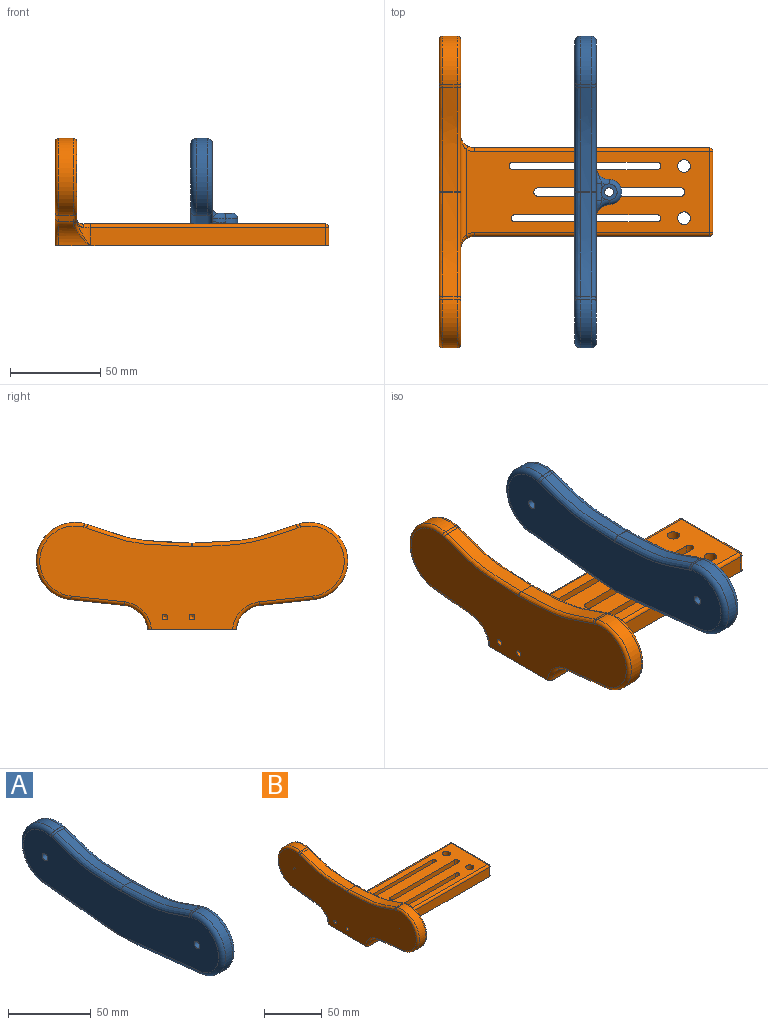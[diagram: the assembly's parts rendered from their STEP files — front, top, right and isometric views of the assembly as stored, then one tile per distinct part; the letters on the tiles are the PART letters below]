
ASSEMBLY  parts=2 mates=1
PART A: 79 faces, bbox 29.6x179.6x56 mm
  f0: plane 2.77x2.26mm, normal (0,0,1), area 2.5mm2, adj f62,f63,f74
  f1: plane 2.77x2.26mm, normal (0,0,1), area 2.5mm2, adj f62,f66,f74
  f2: plane 170.06x45.68mm, normal (1,0,0), area 5187.7mm2, adj f31,f33,f35,f39,f45,f49,f52,f54
  f3: cylinder r=2.4mm len=4.8mm, axis (1,0,0), area 67.9mm2, adj f14,f29
  f4: cylinder r=2.4mm len=4.8mm, axis (1,0,0), area 67.9mm2, adj f14,f21
  f5: cylinder r=21.5mm len=42.88mm, axis (1,0,0), area 423.5mm2, adj f13,f38,f39,f40
  f6: extruded ~6x1.63mm, area 10.2mm2, adj f7,f37,f38,f45
  f7: extruded ~57.91x10.31mm, area 355.5mm2, adj f6,f41,f48,f49
  f8: extruded ~57.91x10.31mm, area 355.5mm2, adj f9,f47,f48,f54
  f9: extruded ~6x1.63mm, area 10.2mm2, adj f8,f51,f55,f56
  f10: cylinder r=21.5mm len=42.88mm, axis (1,0,0), area 423.5mm2, adj f11,f50,f55,f58
  f11: plane 42.81x6mm, normal (0,-0.11,-0.99), area 258.3mm2, adj f10,f12,f46,f60
  f12: plane 49.61x26.59mm, normal (0,0,-1), area 685.2mm2, adj f11,f13,f32,f34,f35,f43,f46,f59
  f13: plane 42.81x6mm, normal (0,0.11,-0.99), area 258.3mm2, adj f5,f12,f35,f43
  f14: plane 167x44.13mm, normal (-1,0,0), area 5335.5mm2, adj f3,f4,f37,f40,f41,f43,f44,f46
  f15: plane 4.18x3mm, normal (0,0.03,1), area 12.6mm2, adj f16,f20,f21,f22
  f16: plane 3.56x3mm, normal (0,-0.85,0.53), area 12.6mm2, adj f15,f17,f21,f22
  f17: plane 3.68x3mm, normal (0,-0.88,-0.47), area 12.6mm2, adj f16,f18,f21,f22
  f18: plane 4.18x3mm, normal (0,-0.03,-1), area 12.6mm2, adj f17,f19,f21,f22
  f19: plane 3.56x3mm, normal (0,0.85,-0.53), area 12.6mm2, adj f18,f20,f21,f22
  f20: plane 3.68x3mm, normal (0,0.88,0.47), area 12.6mm2, adj f15,f19,f21,f22
  f21: plane 8.37x7.37mm, normal (1,0,0), area 27.4mm2, adj f4,f15,f16,f17,f18,f19,f20
  f22: plane 8.37x7.37mm, normal (-1,0,0), area 37mm2, adj f15,f16,f17,f18,f19,f20,f77
  f23: plane 4.18x3mm, normal (0,0.03,-1), area 12.6mm2, adj f24,f28,f29,f30
  f24: plane 3.68x3mm, normal (0,0.88,-0.47), area 12.6mm2, adj f23,f25,f29,f30
  f25: plane 3.56x3mm, normal (0,0.85,0.53), area 12.6mm2, adj f24,f26,f29,f30
  f26: plane 4.18x3mm, normal (0,-0.03,1), area 12.6mm2, adj f25,f27,f29,f30
  f27: plane 3.68x3mm, normal (0,-0.88,0.47), area 12.6mm2, adj f26,f28,f29,f30
  f28: plane 3.56x3mm, normal (0,-0.85,-0.53), area 12.6mm2, adj f23,f27,f29,f30
  f29: plane 8.37x7.37mm, normal (1,0,0), area 27.4mm2, adj f3,f23,f24,f25,f26,f27,f28
  f30: plane 8.37x7.37mm, normal (-1,0,0), area 37mm2, adj f23,f24,f25,f26,f27,f28,f75
  f31: cylinder r=7mm len=7mm, axis (0,0,-1), area 18.2mm2, adj f2,f32,f59,f66
  f32: cylinder r=7mm len=14mm, axis (0,0,1), area 65.3mm2, adj f12,f31,f33,f34,f59,f65
  f33: cylinder r=7mm len=7mm, axis (0,0,1), area 18.2mm2, adj f2,f32,f34,f63
  f34: bspline ~11.74x11.74mm, area 16.8mm2, adj f12,f32,f33,f35
  f35: cylinder r=3mm len=53.31mm, axis (0,0.99,0.11), area 233.2mm2, adj f2,f12,f13,f34,f39
  f36: sphere r=3mm, area 0.4mm2, adj f37,f38,f40
  f37: bspline ~3.6x3.29mm, area 8mm2, adj f6,f14,f36,f41
  f38: cylinder r=3mm len=6mm, axis (1,0,0), area 0.7mm2, adj f5,f6,f36,f42
  f39: torus R=18.5mm, axis (1,0,0), area 315.7mm2, adj f2,f5,f35,f42
  f40: torus R=18.5mm, axis (1,0,0), area 315.7mm2, adj f5,f14,f36,f43
  f41: bspline ~73.35x17.39mm, area 280.6mm2, adj f7,f14,f37,f44
  f42: sphere r=3mm, area 0.4mm2, adj f38,f39,f45
  f43: cylinder r=3mm len=67.35mm, axis (0,-0.99,-0.11), area 249.8mm2, adj f12,f13,f14,f40,f46
  f44: torus R=6mm, axis (1,0,0), area 0.7mm2, adj f14,f41,f47,f48
  f45: bspline ~3.6x3.29mm, area 8mm2, adj f2,f6,f42,f49
  f46: cylinder r=3mm len=67.35mm, axis (0,-0.99,0.11), area 249.8mm2, adj f11,f12,f14,f43,f50
  f47: bspline ~73.35x17.39mm, area 280.6mm2, adj f8,f14,f44,f51
  f48: cylinder r=3mm len=6mm, axis (1,0,0), area 0.7mm2, adj f7,f8,f44,f52
  f49: bspline ~73.35x17.39mm, area 280.6mm2, adj f2,f7,f45,f52
  f50: torus R=18.5mm, axis (1,0,0), area 315.7mm2, adj f10,f14,f46,f53
  f51: bspline ~3.6x3.29mm, area 8mm2, adj f9,f14,f47,f53
  f52: torus R=6mm, axis (1,0,0), area 0.7mm2, adj f2,f48,f49,f54
  f53: sphere r=3mm, area 0.4mm2, adj f50,f51,f55
  f54: bspline ~73.35x17.39mm, area 280.6mm2, adj f2,f8,f52,f56
  f55: cylinder r=3mm len=6mm, axis (1,0,0), area 0.7mm2, adj f9,f10,f53,f57
  f56: bspline ~3.6x3.29mm, area 8mm2, adj f2,f9,f54,f57
  f57: sphere r=3mm, area 0.4mm2, adj f55,f56,f58
  f58: torus R=18.5mm, axis (1,0,0), area 315.7mm2, adj f2,f10,f57,f60
  f59: bspline ~8.63x7.79mm, area 16.8mm2, adj f12,f31,f32,f60
  f60: cylinder r=3mm len=53.31mm, axis (0,0.99,-0.11), area 233.2mm2, adj f2,f11,f12,f58,f59
  f61: bspline ~9.6x6mm, area 17.3mm2, adj f2,f62,f63
  f62: cylinder r=3mm len=9.67mm, axis (0,-1,0), area 45.6mm2, adj f0,f1,f2,f61,f64,f72
  f63: torus R=10mm, axis (0,0,1), area 30.5mm2, adj f0,f33,f61,f65,f74
  f64: bspline ~10.85x6mm, area 15.9mm2, adj f2,f62,f66
  f65: torus R=4mm, axis (0,0,1), area 80.8mm2, adj f32,f63,f66,f74
  f66: torus R=10mm, axis (0,0,1), area 30.5mm2, adj f1,f31,f64,f65,f74
  f67: cone r=0mm half-angle=59deg, axis (0,0,-1), area 5.7mm2, adj f68
  f68: cylinder r=1.25mm len=20mm, axis (0,0,-1), area 157.1mm2, adj f12,f67
  f69: cone r=0mm half-angle=59deg, axis (0,0,-1), area 5.7mm2, adj f70
  f70: cylinder r=1.25mm len=20mm, axis (0,0,-1), area 157.1mm2, adj f12,f69
  f71: cylinder r=2.4mm len=4.8mm, axis (0,0,1), area 30.2mm2, adj f12,f73
  f72: plane 4.12x0.5mm, normal (0,0,-1), area 1.4mm2, adj f62,f74
  f73: plane 9x9mm, normal (0,0,1), area 45.5mm2, adj f71,f74
  f74: cylinder r=4.5mm len=9mm, axis (0,0,1), area 112.4mm2, adj f0,f1,f63,f65,f66,f72,f73
  f75: cylinder r=1.65mm len=3.75mm, axis (1,0,0), area 38.9mm2, adj f30,f76
  f76: plane 3.3x3.3mm, normal (-1,0,0), area 8.6mm2, adj f75
  f77: cylinder r=1.65mm len=3.75mm, axis (1,0,0), area 38.9mm2, adj f22,f78
  f78: plane 3.3x3.3mm, normal (-1,0,0), area 8.6mm2, adj f77
PART B: 119 faces, bbox 152.2x176.7x62.8 mm
  f0: plane 152.18x49.18mm, normal (0,0,-1), area 5791.1mm2, adj f22,f44,f45,f46,f47,f48,f52,f53
  f1: plane 80.1x8.8mm, normal (0,-1,0), area 704.9mm2, adj f2,f4,f13,f68
  f2: cylinder r=2mm len=8.8mm, axis (0,0,-1), area 55.3mm2, adj f1,f3,f13,f68
  f3: plane 80.1x8.8mm, normal (0,1,0), area 704.9mm2, adj f2,f4,f13,f68
  f4: cylinder r=2mm len=8.8mm, axis (0,0,-1), area 55.3mm2, adj f1,f3,f13,f68
  f5: cylinder r=2.4mm len=8.8mm, axis (0,0,-1), area 66.4mm2, adj f6,f8,f13,f63
  f6: plane 79x8.8mm, normal (0,1,0), area 695.2mm2, adj f5,f7,f13,f63
  f7: cylinder r=2.4mm len=8.8mm, axis (0,0,-1), area 66.4mm2, adj f6,f8,f13,f63
  f8: plane 79x8.8mm, normal (0,-1,0), area 695.2mm2, adj f5,f7,f13,f63
  f9: plane 79x8.8mm, normal (0,-1,0), area 695.2mm2, adj f10,f12,f13,f58
  f10: cylinder r=2mm len=8.8mm, axis (0,0,-1), area 55.3mm2, adj f9,f11,f13,f58
  f11: plane 79x8.8mm, normal (0,1,0), area 695.2mm2, adj f10,f12,f13,f58
  f12: cylinder r=2mm len=8.8mm, axis (0,0,-1), area 55.3mm2, adj f9,f11,f13,f58
  f13: plane 135x47.27mm, normal (0,0,1), area 4942.5mm2, adj f1,f2,f3,f4,f5,f6,f7,f8
  f14: extruded ~57.92x10.32mm, area 474.1mm2, adj f15,f80,f84,f85
  f15: extruded ~8x1.65mm, area 13.7mm2, adj f14,f77,f78,f81
  f16: cylinder r=21.5mm len=42.88mm, axis (1,0,0), area 564.8mm2, adj f17,f73,f76,f77
  f17: plane 29.49x8mm, normal (0,-0.11,-0.99), area 237.3mm2, adj f16,f47,f71,f74
  f18: plane 29.49x8mm, normal (0,0.11,-0.99), area 237.3mm2, adj f19,f48,f87,f97
  f19: cylinder r=21.5mm len=42.88mm, axis (1,0,0), area 564.8mm2, adj f18,f90,f94,f96
  f20: extruded ~8x1.65mm, area 13.7mm2, adj f21,f89,f93,f94
  f21: extruded ~57.92x10.32mm, area 474.1mm2, adj f20,f85,f86,f91
  f22: plane 169x57.5mm, normal (-1,0,0), area 6397.8mm2, adj f0,f69,f71,f73,f78,f80,f82,f83
  f23: plane 169x43.68mm, normal (1,0,0), area 5600.3mm2, adj f24,f25,f49,f50,f51,f72,f74,f76
  f24: cylinder r=2.4mm len=4.8mm, axis (1,0,0), area 67.9mm2, adj f23,f33
  f25: cylinder r=2.4mm len=4.8mm, axis (1,0,0), area 67.9mm2, adj f23,f42
  f26: plane 4.18x3mm, normal (0,0.03,-1), area 12.6mm2, adj f27,f31,f32,f33
  f27: plane 3.68x3mm, normal (0,0.88,-0.47), area 12.6mm2, adj f26,f28,f32,f33
  f28: plane 3.56x3mm, normal (0,0.85,0.53), area 12.6mm2, adj f27,f29,f32,f33
  f29: plane 4.18x3mm, normal (0,-0.03,1), area 12.6mm2, adj f28,f30,f32,f33
  f30: plane 3.68x3mm, normal (0,-0.88,0.47), area 12.6mm2, adj f29,f31,f32,f33
  f31: plane 3.56x3mm, normal (0,-0.85,-0.53), area 12.6mm2, adj f26,f30,f32,f33
  f32: plane 8.37x7.37mm, normal (1,0,0), area 27.4mm2, adj f26,f27,f28,f29,f30,f31,f34
  f33: plane 8.37x7.37mm, normal (-1,0,0), area 27.4mm2, adj f24,f26,f27,f28,f29,f30,f31
  f34: cone r=0mm half-angle=59deg, axis (1,0,0), area 11.1mm2, adj f32,f117
  f35: plane 4.18x3mm, normal (0,0.03,1), area 12.6mm2, adj f36,f40,f41,f42
  f36: plane 3.56x3mm, normal (0,-0.85,0.53), area 12.6mm2, adj f35,f37,f41,f42
  f37: plane 3.68x3mm, normal (0,-0.88,-0.47), area 12.6mm2, adj f36,f38,f41,f42
  f38: plane 4.18x3mm, normal (0,-0.03,-1), area 12.6mm2, adj f37,f39,f41,f42
  f39: plane 3.56x3mm, normal (0,0.85,-0.53), area 12.6mm2, adj f38,f40,f41,f42
  f40: plane 3.68x3mm, normal (0,0.88,0.47), area 12.6mm2, adj f35,f39,f41,f42
  f41: plane 8.37x7.37mm, normal (1,0,0), area 27.4mm2, adj f35,f36,f37,f38,f39,f40,f43
  f42: plane 8.37x7.37mm, normal (-1,0,0), area 27.4mm2, adj f25,f35,f36,f37,f38,f39,f40
  f43: cone r=0mm half-angle=59deg, axis (1,0,0), area 11.1mm2, adj f41,f115
  f44: plane 130.53x10.03mm, normal (0,-1,0), area 1305mm2, adj f0,f50,f70,f106,f108
  f45: plane 130.53x10.03mm, normal (0,1,0), area 1305mm2, adj f0,f49,f99,f102,f103
  f46: plane 45x10mm, normal (1,0,0), area 450mm2, adj f0,f103,f105,f106
  f47: cylinder r=15mm len=17.07mm, axis (-1,0,0), area 212.3mm2, adj f0,f17,f69,f70,f72
  f48: cylinder r=15mm len=17.07mm, axis (-1,0,0), area 212.3mm2, adj f0,f18,f83,f98,f99
  f49: cylinder r=7.5mm len=14.9mm, axis (0,0,1), area 44.9mm2, adj f23,f45,f99,f100,f101
  f50: cylinder r=7.5mm len=14.9mm, axis (0,0,1), area 44.9mm2, adj f23,f44,f70,f109,f110
  f51: cylinder r=3mm len=64mm, axis (0,1,0), area 262.2mm2, adj f13,f23,f100,f110
  f52: cylinder r=3.5mm len=12mm, axis (0,0,-1), area 263.9mm2, adj f0,f13
  f53: cylinder r=3.5mm len=12mm, axis (0,0,-1), area 263.9mm2, adj f0,f13
  f54: plane 79x3.2mm, normal (0,-1,0), area 252.8mm2, adj f0,f55,f57,f58
  f55: cylinder r=2.85mm len=5.7mm, axis (0,0,-1), area 28.7mm2, adj f0,f54,f56,f58
  f56: plane 79x3.2mm, normal (0,1,0), area 252.8mm2, adj f0,f55,f57,f58
  f57: cylinder r=2.85mm len=5.7mm, axis (0,0,-1), area 28.7mm2, adj f0,f54,f56,f58
  f58: plane 84.7x5.7mm, normal (0,0,-1), area 147.3mm2, adj f9,f10,f11,f12,f54,f55,f56,f57
  f59: cylinder r=3.65mm len=7.3mm, axis (0,0,-1), area 36.7mm2, adj f0,f60,f62,f63
  f60: plane 79x3.2mm, normal (0,-1,0), area 252.8mm2, adj f0,f59,f61,f63
  f61: cylinder r=3.65mm len=7.3mm, axis (0,0,-1), area 36.7mm2, adj f0,f60,f62,f63
  f62: plane 79x3.2mm, normal (0,1,0), area 252.8mm2, adj f0,f59,f61,f63
  f63: plane 86.3x7.3mm, normal (0,0,-1), area 221.3mm2, adj f5,f6,f7,f8,f59,f60,f61,f62
  f64: plane 80.1x3.2mm, normal (0,-1,0), area 256.3mm2, adj f0,f65,f67,f68
  f65: cylinder r=2.85mm len=5.7mm, axis (0,0,-1), area 28.7mm2, adj f0,f64,f66,f68
  f66: plane 80.1x3.2mm, normal (0,1,0), area 256.3mm2, adj f0,f65,f67,f68
  f67: cylinder r=2.85mm len=5.7mm, axis (0,0,-1), area 28.7mm2, adj f0,f64,f66,f68
  f68: plane 85.8x5.7mm, normal (0,0,-1), area 149.1mm2, adj f1,f2,f3,f4,f64,f65,f66,f67
  f69: torus R=17mm, axis (1,0,0), area 67.7mm2, adj f0,f22,f47,f71
  f70: bspline ~14.67x10.23mm, area 31.2mm2, adj f0,f44,f47,f50,f72
  f71: cylinder r=2mm len=29.71mm, axis (0,-0.99,0.11), area 93.2mm2, adj f17,f22,f69,f73
  f72: torus R=17mm, axis (1,0,0), area 17mm2, adj f23,f47,f70,f74
  f73: torus R=19.5mm, axis (1,0,0), area 214.3mm2, adj f16,f22,f71,f75
  f74: cylinder r=2mm len=29.71mm, axis (0,0.99,-0.11), area 93.2mm2, adj f17,f23,f72,f76
  f75: sphere r=2mm, area 0.2mm2, adj f73,f77,f78
  f76: torus R=19.5mm, axis (1,0,0), area 214.3mm2, adj f16,f23,f74,f79
  f77: cylinder r=2mm len=8mm, axis (1,0,0), area 0.6mm2, adj f15,f16,f75,f79
  f78: bspline ~2.98x2.64mm, area 5.4mm2, adj f15,f22,f75,f80
  f79: sphere r=2mm, area 0.2mm2, adj f76,f77,f81
  f80: bspline ~75.96x16.5mm, area 186.8mm2, adj f14,f22,f78,f82
  f81: bspline ~2.71x2.56mm, area 5.4mm2, adj f15,f23,f79,f84
  f82: torus R=4mm, axis (1,0,0), area 0.3mm2, adj f22,f80,f85,f86
  f83: torus R=17mm, axis (1,0,0), area 67.7mm2, adj f0,f22,f48,f87
  f84: bspline ~75.96x16.5mm, area 186.8mm2, adj f14,f23,f81,f88
  f85: cylinder r=2mm len=8mm, axis (1,0,0), area 0.6mm2, adj f14,f21,f82,f88
  f86: bspline ~75.96x16.5mm, area 186.8mm2, adj f21,f22,f82,f89
  f87: cylinder r=2mm len=29.71mm, axis (0,-0.99,-0.11), area 93.2mm2, adj f18,f22,f83,f90
  f88: torus R=4mm, axis (1,0,0), area 0.3mm2, adj f23,f84,f85,f91
  f89: bspline ~2.71x2.56mm, area 5.4mm2, adj f20,f22,f86,f92
  f90: torus R=19.5mm, axis (1,0,0), area 214.3mm2, adj f19,f22,f87,f92
  f91: bspline ~75.96x16.5mm, area 186.8mm2, adj f21,f23,f88,f93
  f92: sphere r=2mm, area 0.2mm2, adj f89,f90,f94
  f93: bspline ~2.98x2.64mm, area 5.4mm2, adj f20,f23,f91,f95
  f94: cylinder r=2mm len=8mm, axis (1,0,0), area 0.6mm2, adj f19,f20,f92,f95
  f95: sphere r=2mm, area 0.2mm2, adj f93,f94,f96
  f96: torus R=19.5mm, axis (1,0,0), area 214.3mm2, adj f19,f23,f95,f97
  f97: cylinder r=2mm len=29.71mm, axis (0,0.99,0.11), area 93.2mm2, adj f18,f23,f96,f98
  f98: torus R=17mm, axis (1,0,0), area 17mm2, adj f23,f48,f97,f99
  f99: bspline ~14.67x10.23mm, area 31.2mm2, adj f0,f45,f48,f49,f98
  f100: bspline ~8.83x5mm, area 9.6mm2, adj f49,f51,f101
  f101: torus R=9.5mm, axis (0,0,1), area 12.8mm2, adj f13,f49,f100,f102
  f102: cylinder r=2mm len=130.5mm, axis (1,0,0), area 410mm2, adj f13,f45,f101,f104
  f103: cylinder r=2mm len=10mm, axis (0,0,-1), area 31.4mm2, adj f0,f45,f46,f104
  f104: sphere r=2mm, area 4mm2, adj f102,f103,f105
  f105: cylinder r=2mm len=45mm, axis (0,1,0), area 141.4mm2, adj f13,f46,f104,f107
  f106: cylinder r=2mm len=10mm, axis (0,0,1), area 31.4mm2, adj f0,f44,f46,f107
  f107: sphere r=2mm, area 6.3mm2, adj f105,f106,f108
  f108: cylinder r=2mm len=130.5mm, axis (-1,0,0), area 410mm2, adj f13,f44,f107,f109
  f109: torus R=9.5mm, axis (0,0,1), area 12.8mm2, adj f13,f50,f108,f110
  f110: bspline ~8.83x5mm, area 9.5mm2, adj f50,f51,f109
  f111: cone r=0mm half-angle=59deg, axis (-1,0,0), area 10mm2, adj f112
  f112: cylinder r=1.65mm len=20mm, axis (-1,0,0), area 207.3mm2, adj f22,f111
  f113: cone r=0mm half-angle=59deg, axis (-1,0,0), area 10mm2, adj f114
  f114: cylinder r=1.65mm len=20mm, axis (-1,0,0), area 207.3mm2, adj f22,f113
  f115: cylinder r=1.65mm len=3.3mm, axis (-1,0,0), area 34.2mm2, adj f43,f116
  f116: plane 3.3x3.3mm, normal (1,0,0), area 8.6mm2, adj f115
  f117: cylinder r=1.65mm len=3.3mm, axis (-1,0,0), area 34.2mm2, adj f34,f118
  f118: plane 3.3x3.3mm, normal (1,0,0), area 8.6mm2, adj f117
PLACE A rot(axis=(0,0,1),0deg) t=(0.74,-26.83,-55.83)mm
PLACE B t=(-74.62,-26.83,-55.83)mm fixed
MATE pin_slot B.f5 <-> A.f32  axis (0,0,1) through (47.38,-26.83,-55.83)mm
